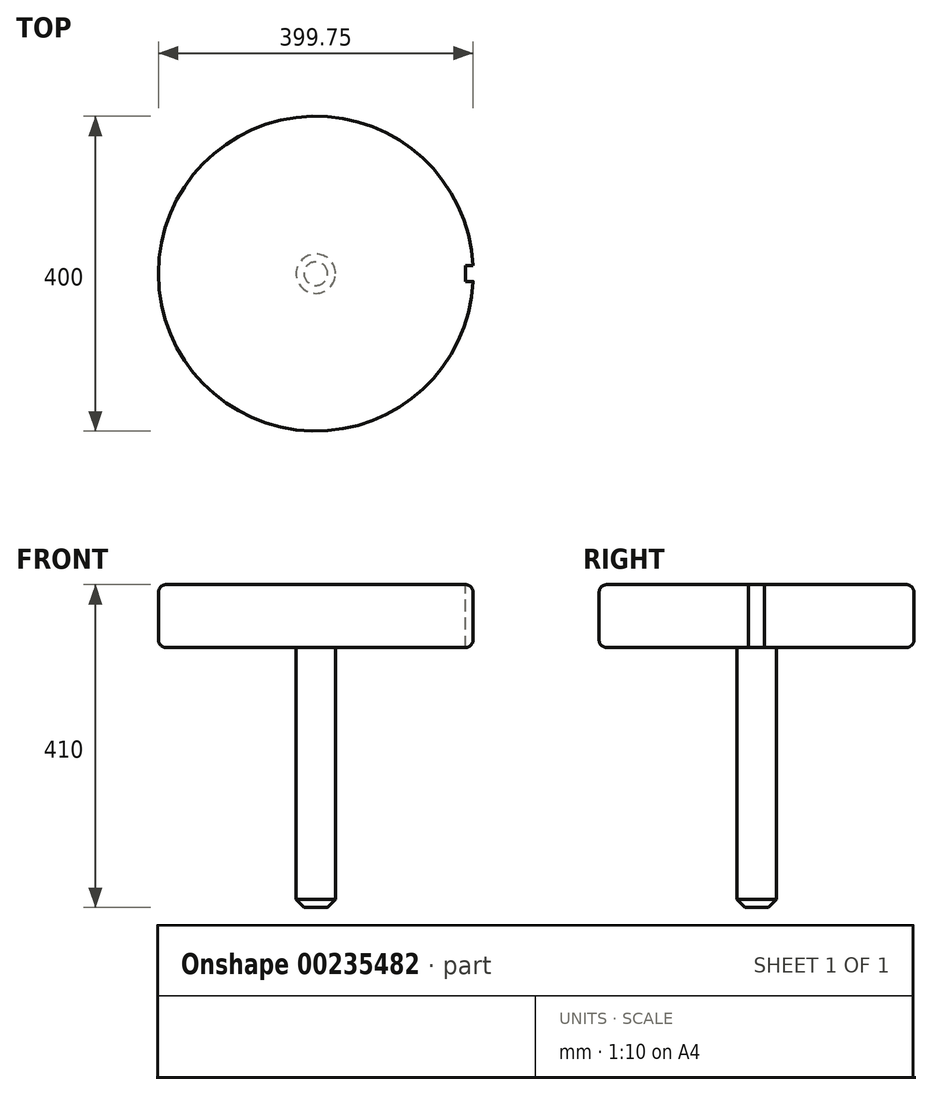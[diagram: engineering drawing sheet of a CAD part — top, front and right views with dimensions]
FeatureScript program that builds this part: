
annotation { "Feature Type Name" : "Feature", "Feature Type Description" : "" }
export const myFeature = defineFeature(function(context is Context, id is Id, definition is map)
    precondition{}
    {
        {
            var Q0;
            Q0=qCreatedBy(makeId("Top.planeOp"),FACE);
            var sketch = newSketch(context, id + "F0", { "sketchPlane" : qUnion([Q0])});
            skCircle(sketch, "E0", {"center": v(0, 0) * mm, "radius": 200 * mm});
            skSolve(sketch);
        }
        {
            var Q0;
            Q0 = qSketchRegion(id + "F0", true);
            extrude(context, id + "F1", {"entities" : qUnion([Q0]), "depth" : 80 * mm});
        }
        {
            var Q0;
            Q0=makeQuery(id+"F1.opExtrude","CAP_FACE",FACE,{"disambiguationData":[OSD([sQuery(id+"F0.wireOp",EDGE,"E0")])],"isStart":false});
            var Q1;
            Q1=makeQuery(id+"F1.opExtrude","CAP_FACE",FACE,{"disambiguationData":[OSD([sQuery(id+"F0.wireOp",EDGE,"E0")])],"isStart":true});
            fillet(context, id + "F2", {"entities" : qUnion([Q0, Q1]), "radius" : 10 * mm, "tangentPropagation" : true, "allowEdgeOverflow" : false});
        }
        {
            var Q0;
            Q0=qCreatedBy(makeId("Right.planeOp"),FACE);
            var sketch = newSketch(context, id + "F3", { "sketchPlane" : qUnion([Q0])});
            skLineSegment(sketch, "E1", {"start": v(0, 0) * mm, "end": v(0, -330) * mm});
            skLineSegment(sketch, "E2", {"start": v(0, -330) * mm, "end": v(-25, -330) * mm});
            skLineSegment(sketch, "E3", {"start": v(-25, -320) * mm, "end": v(-25, 0) * mm});
            skLineSegment(sketch, "E4", {"start": v(-25, 0) * mm, "end": v(0, 0) * mm});
            skLineSegment(sketch, "E5", {"start": v(-25, -320) * mm, "end": v(-15, -330) * mm});
            skLineSegment(sketch, "E6", {"start": v(-15, -330) * mm, "end": v(-25, -330) * mm, "construction": true});
            skSolve(sketch);
        }
        {
            var Q0;
            Q0 = qSketchRegion(id + "F3", true);
            var Q1;
            Q1=sQuery(id+"F3.wireOp",EDGE,"E1");
            revolve(context, id + "F4", {"operationType" : NewBodyOperationType.ADD, "entities" : qUnion([Q0]), "axis" : qUnion([Q1]), "revolveType" : RevolveType.FULL});
        }
        {
            var Q0;
            Q0=makeQuery(id+"F1.opExtrude","CAP_FACE",FACE,{"disambiguationData":[OSD([sQuery(id+"F0.wireOp",EDGE,"E0")])],"isStart":false});
            var sketch = newSketch(context, id + "F5", { "sketchPlane" : qUnion([Q0])});
            skLineSegment(sketch, "E7.bottom", {"start": v(190, -10) * mm, "end": v(210, -10) * mm});
            skLineSegment(sketch, "E7.top", {"start": v(190, 10) * mm, "end": v(210, 10) * mm});
            skLineSegment(sketch, "E7.left", {"start": v(190, -10) * mm, "end": v(190, 10) * mm});
            skLineSegment(sketch, "E7.right", {"start": v(210, -10) * mm, "end": v(210, 10) * mm});
            skPoint(sketch, "E7.middle", {"position": v(200, 0) * mm});
            skSolve(sketch);
        }
        {
            var Q0;
            Q0 = qSketchRegion(id + "F5", true);
            var Q1;
            Q1=makeQuery(id+"F1.opExtrude","CAP_FACE",FACE,{"disambiguationData":[OSD([sQuery(id+"F0.wireOp",EDGE,"E0")])],"isStart":true});
            extrude(context, id + "F6", {"entities" : qUnion([Q0]), "operationType" : NewBodyOperationType.REMOVE, "endBound" : BoundingType.UP_TO_SURFACE, "oppositeDirection" : true, "endBoundEntityFace" : qUnion([Q1]), "depth" : 25 * mm});
        }
    });
